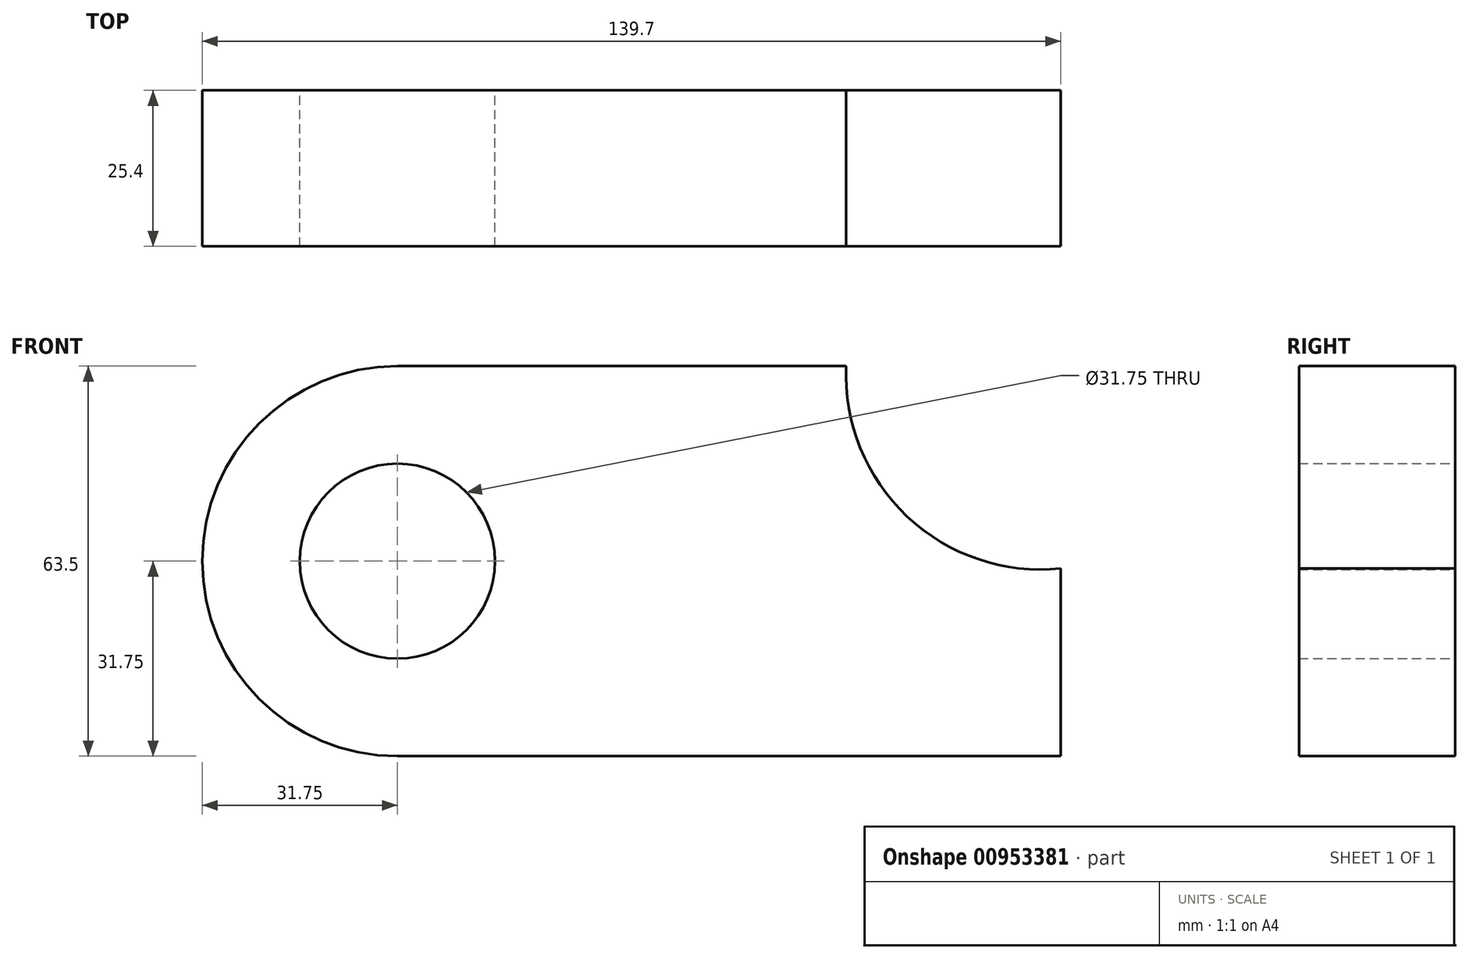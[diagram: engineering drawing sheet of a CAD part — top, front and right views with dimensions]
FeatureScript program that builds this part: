
annotation { "Feature Type Name" : "Feature", "Feature Type Description" : "" }
export const myFeature = defineFeature(function(context is Context, id is Id, definition is map)
    precondition{}
    {
        {
            var Q0;
            Q0=qCreatedBy(makeId("Front.planeOp"),FACE);
            var sketch = newSketch(context, id + "F0", { "sketchPlane" : qUnion([Q0])});
            skLineSegment(sketch, "E0", {"start": v(0, 0) * mm, "end": v(107.95, 0) * mm});
            skLineSegment(sketch, "E1", {"start": v(0, 0) * mm, "end": v(0, 63.5) * mm});
            skLineSegment(sketch, "E2", {"start": v(0, 63.5) * mm, "end": v(73.03, 63.5) * mm});
            skLineSegment(sketch, "E3", {"start": v(107.95, 0) * mm, "end": v(107.95, 30.54) * mm});
            skArc(sketch, "E4", {"start": v(73.03, 63.5) * mm, "mid": v(82.95, 39.04) * mm, "end": v(107.95, 30.54) * mm});
            skCircle(sketch, "E5", {"center": v(0, 31.75) * mm, "radius": 15.88 * mm});
            skArc(sketch, "E6", {"start": v(0, 63.5) * mm, "mid": v(-31.75, 31.75) * mm, "end": v(0, 0) * mm});
            skSolve(sketch);
        }
        {
            var Q0;
            {var subQ5=sQuery(id+"F0.wireOp",EDGE,"E0");Q0=makeQuery(id+"F0.imprint","IMPRINT",FACE,{"disambiguationData":[TD([[makeQuery(id+"F0.imprint","IMPRINT",EDGE,{"derivedFrom":subQ5}),1.0]])]});}
            var Q1;
            {var subQ0=sQuery(id+"F0.wireOp",EDGE,"E6");Q1=makeQuery(id+"F0.imprint","IMPRINT",FACE,{"disambiguationData":[TD([[makeQuery(id+"F0.imprint","IMPRINT",EDGE,{"derivedFrom":subQ0}),1.0]])]});}
            extrude(context, id + "F1", {"entities" : qUnion([Q0, Q1]), "depth" : 25.4 * mm, "offsetDistance" : 25.4 * mm});
        }
    });
